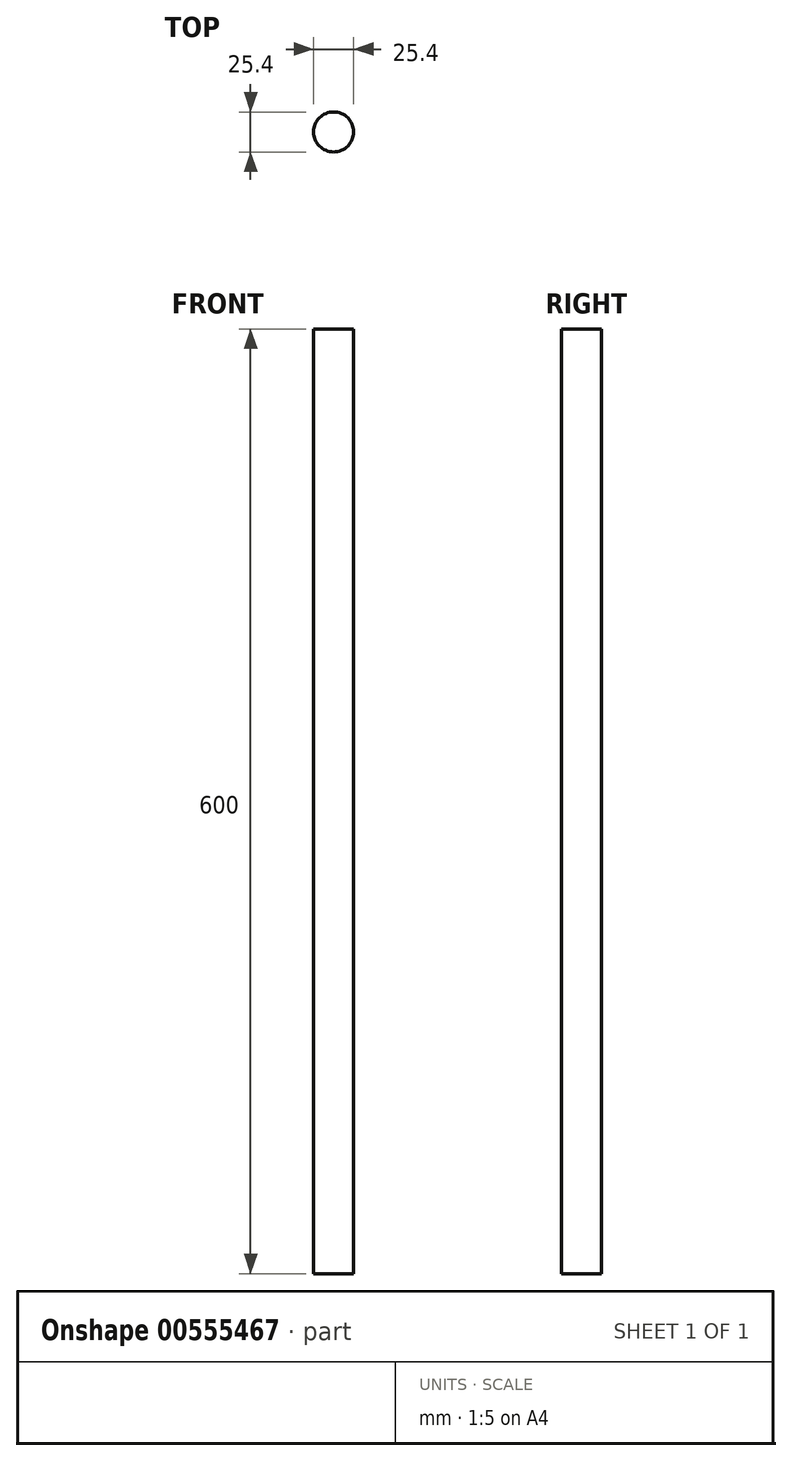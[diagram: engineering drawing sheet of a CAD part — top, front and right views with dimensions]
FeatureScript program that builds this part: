
annotation { "Feature Type Name" : "Feature", "Feature Type Description" : "" }
export const myFeature = defineFeature(function(context is Context, id is Id, definition is map)
    precondition{}
    {
        {
            var Q0;
            Q0=qCreatedBy(makeId("Top.planeOp"),FACE);
            var sketch = newSketch(context, id + "F0", { "sketchPlane" : qUnion([Q0])});
            skCircle(sketch, "E0", {"center": v(0, 0) * mm, "radius": 12.7 * mm});
            skSolve(sketch);
        }
        {
            var Q0;
            Q0=qSketchRegion(id+"F0",true);
            extrude(context, id + "F1", {"entities" : qUnion([Q0]), "depth" : 600 * mm, "offsetDistance" : 25.4 * mm});
        }
    });
